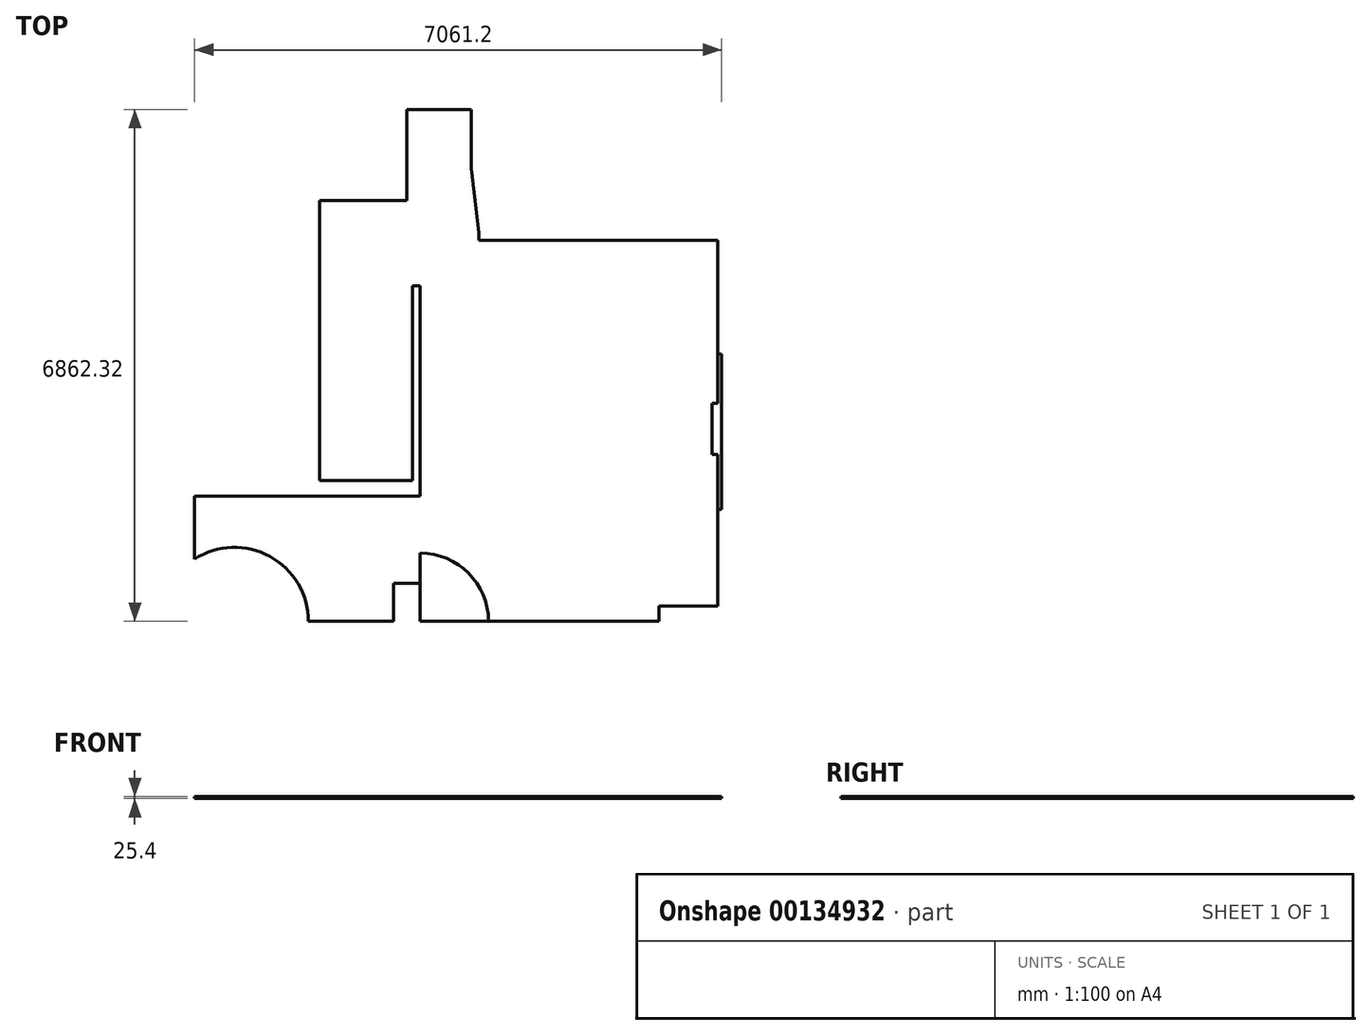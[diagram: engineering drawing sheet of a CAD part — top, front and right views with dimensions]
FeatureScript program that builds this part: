
annotation { "Feature Type Name" : "Feature", "Feature Type Description" : "" }
export const myFeature = defineFeature(function(context is Context, id is Id, definition is map)
    precondition{}
    {
        {
            var Q0;
            Q0=qCreatedBy(makeId("Top.planeOp"),FACE);
            var sketch = newSketch(context, id + "F0", { "sketchPlane" : qUnion([Q0])});
            skLineSegment(sketch, "E0.bottom", {"start": v(3200.4, 0) * mm, "end": v(0, 0) * mm});
            skLineSegment(sketch, "E0.top", {"start": v(3987.8, 5105.4) * mm, "end": v(787.4, 5105.4) * mm});
            skLineSegment(sketch, "E0.left", {"start": v(3987.8, 203.2) * mm, "end": v(3987.8, 5105.4) * mm});
            skLineSegment(sketch, "E0.right", {"start": v(0, 0) * mm, "end": v(0, 508) * mm});
            skLineSegment(sketch, "E1.bottom", {"start": v(-355.6, 0) * mm, "end": v(-3022.6, 0) * mm});
            skLineSegment(sketch, "E1.top", {"start": v(0, 1676.4) * mm, "end": v(-3022.6, 1676.4) * mm});
            skLineSegment(sketch, "E1.left", {"start": v(-355.6, 0) * mm, "end": v(-355.6, 508) * mm});
            skLineSegment(sketch, "E1.right", {"start": v(-3022.6, 0) * mm, "end": v(-3022.6, 1676.4) * mm});
            skLineSegment(sketch, "E2", {"start": v(-355.6, 508) * mm, "end": v(0, 508) * mm});
            skLineSegment(sketch, "E3", {"start": v(3200.4, 0) * mm, "end": v(3200.4, 203.2) * mm});
            skLineSegment(sketch, "E4", {"start": v(3200.4, 203.2) * mm, "end": v(3987.8, 203.2) * mm});
            skLineSegment(sketch, "E5", {"start": v(3987.8, 2235.2) * mm, "end": v(3911.6, 2235.2) * mm});
            skLineSegment(sketch, "E6", {"start": v(3911.6, 2235.2) * mm, "end": v(3911.6, 2921) * mm});
            skLineSegment(sketch, "E7", {"start": v(3911.6, 2921) * mm, "end": v(3987.8, 2921) * mm});
            skLineSegment(sketch, "E8", {"start": v(3987.8, 3581.4) * mm, "end": v(4038.6, 3581.4) * mm});
            skLineSegment(sketch, "E9", {"start": v(4038.6, 3581.4) * mm, "end": v(4038.6, 1498.6) * mm});
            skLineSegment(sketch, "E10", {"start": v(4038.6, 1498.6) * mm, "end": v(3987.8, 1498.6) * mm});
            skLineSegment(sketch, "E11.bottom", {"start": v(685.8, 9550.4) * mm, "end": v(3962.4, 9550.4) * mm});
            skLineSegment(sketch, "E11.top", {"start": v(787.4, 5207) * mm, "end": v(3962.4, 5207) * mm});
            skLineSegment(sketch, "E11.right", {"start": v(3962.4, 9550.4) * mm, "end": v(3962.4, 5207) * mm});
            skLineSegment(sketch, "E12", {"start": v(1778, 5207) * mm, "end": v(1778, 5969) * mm});
            skLineSegment(sketch, "E13", {"start": v(1778, 5969) * mm, "end": v(1981.2, 5969) * mm});
            skLineSegment(sketch, "E14", {"start": v(1981.2, 5969) * mm, "end": v(1981.2, 5207) * mm});
            skLineSegment(sketch, "E15", {"start": v(3810, 5969) * mm, "end": v(3810, 5207) * mm});
            skLineSegment(sketch, "E16", {"start": v(685.8, 9550.4) * mm, "end": v(685.8, 6070.6) * mm});
            skLineSegment(sketch, "E17", {"start": v(685.8, 6070.6) * mm, "end": v(787.4, 5207) * mm});
            skLineSegment(sketch, "E18", {"start": v(787.4, 5207) * mm, "end": v(787.4, 5105.4) * mm});
            skArc(sketch, "E19", {"start": v(701.33, 5938.55) * mm, "mid": v(1276.88, 5757.44) * mm, "end": v(1524, 5207) * mm});
            skLineSegment(sketch, "E20.bottom", {"start": v(-3505.2, 10033) * mm, "end": v(-76.2, 10033) * mm});
            skLineSegment(sketch, "E20.top", {"start": v(-3505.2, 5740.4) * mm, "end": v(-2108.2, 5740.4) * mm});
            skLineSegment(sketch, "E20.left", {"start": v(-3505.2, 10033) * mm, "end": v(-3505.2, 5740.4) * mm});
            skLineSegment(sketch, "E20.right", {"start": v(-177.8, 8839.2) * mm, "end": v(-177.8, 5740.4) * mm});
            skLineSegment(sketch, "E21", {"start": v(-2514.6, 10033) * mm, "end": v(-2514.6, 10083.8) * mm});
            skLineSegment(sketch, "E22", {"start": v(-2514.6, 10083.8) * mm, "end": v(-1028.7, 10083.8) * mm});
            skLineSegment(sketch, "E23", {"start": v(-1028.7, 10083.8) * mm, "end": v(-1028.7, 10033) * mm});
            skLineSegment(sketch, "E24", {"start": v(-2057.4, 10033) * mm, "end": v(-2057.4, 9956.8) * mm});
            skLineSegment(sketch, "E25", {"start": v(-2057.4, 9956.8) * mm, "end": v(-1397, 9956.8) * mm});
            skLineSegment(sketch, "E26", {"start": v(-1397, 9956.8) * mm, "end": v(-1397, 10033) * mm});
            skArc(sketch, "E27", {"start": v(-1498.6, 0) * mm, "mid": v(-2013.33, 868.81) * mm, "end": v(-3022.6, 834.73) * mm});
            skLineSegment(sketch, "E28.bottom", {"start": v(-3840.05, 5638.8) * mm, "end": v(-2108.2, 5638.8) * mm});
            skLineSegment(sketch, "E28.top", {"start": v(-3840.05, 3964.94) * mm, "end": v(-1447.8, 3964.94) * mm});
            skLineSegment(sketch, "E28.left", {"start": v(-3840.05, 5638.8) * mm, "end": v(-3840.05, 3964.94) * mm});
            skLineSegment(sketch, "E28.right", {"start": v(-1447.8, 5638.8) * mm, "end": v(-1447.8, 3964.94) * mm});
            skLineSegment(sketch, "E29.top", {"start": v(-1346.2, 1888.18) * mm, "end": v(-101.6, 1888.18) * mm});
            skLineSegment(sketch, "E29.left", {"start": v(-1346.2, 5638.8) * mm, "end": v(-1346.2, 1888.18) * mm});
            skLineSegment(sketch, "E29.right", {"start": v(-101.6, 4495.8) * mm, "end": v(-101.6, 1888.18) * mm});
            skLineSegment(sketch, "E30.bottom", {"start": v(-3989.7, 1923.09) * mm, "end": v(-1601.5, 1923.09) * mm});
            skLineSegment(sketch, "E30.top", {"start": v(-3989.7, 3685.8) * mm, "end": v(-1601.5, 3685.8) * mm});
            skLineSegment(sketch, "E30.left", {"start": v(-3989.7, 1923.09) * mm, "end": v(-3989.7, 3685.8) * mm});
            skLineSegment(sketch, "E30.right", {"start": v(-1601.5, 1923.09) * mm, "end": v(-1601.5, 3685.8) * mm});
            skLineSegment(sketch, "E31.trimOffspring", {"start": v(0, 1676.4) * mm, "end": v(0, 4495.8) * mm});
            skLineSegment(sketch, "E32", {"start": v(-101.6, 4495.8) * mm, "end": v(0, 4495.8) * mm});
            skLineSegment(sketch, "E33", {"start": v(-1346.2, 5638.8) * mm, "end": v(-177.8, 5638.8) * mm});
            skArc(sketch, "E34", {"start": v(-177.8, 6477) * mm, "mid": v(-698.65, 6261.25) * mm, "end": v(-914.4, 5740.4) * mm});
            skLineSegment(sketch, "E35", {"start": v(-177.8, 6862.32) * mm, "end": v(685.8, 6862.32) * mm});
            skLineSegment(sketch, "E36", {"start": v(-2108.2, 5638.8) * mm, "end": v(-2108.2, 5740.4) * mm});
            skLineSegment(sketch, "E37", {"start": v(-1498.6, 5638.8) * mm, "end": v(-1498.6, 5740.4) * mm});
            skLineSegment(sketch, "E38", {"start": v(-177.8, 5740.4) * mm, "end": v(-177.8, 5638.8) * mm});
            skLineSegment(sketch, "E39.trimOffspring", {"start": v(-1498.6, 5740.4) * mm, "end": v(-177.8, 5740.4) * mm});
            skLineSegment(sketch, "E40.trimOffspring", {"start": v(-1498.6, 5638.8) * mm, "end": v(-1447.8, 5638.8) * mm});
            skLineSegment(sketch, "E41", {"start": v(-1447.8, 5638.8) * mm, "end": v(-1346.2, 5638.8) * mm, "construction": true});
            skLineSegment(sketch, "E42.bottom", {"start": v(-177.8, 8839.2) * mm, "end": v(244.03, 8839.2) * mm});
            skLineSegment(sketch, "E42.top", {"start": v(-177.8, 7035.8) * mm, "end": v(244.03, 7035.8) * mm});
            skLineSegment(sketch, "E42.left", {"start": v(-177.8, 8839.2) * mm, "end": v(-177.8, 7035.8) * mm});
            skLineSegment(sketch, "E42.right", {"start": v(244.03, 8839.2) * mm, "end": v(244.03, 7035.8) * mm});
            skLineSegment(sketch, "E43.trimOffspring", {"start": v(3810, 5969) * mm, "end": v(3962.4, 5969) * mm});
            skLineSegment(sketch, "E44", {"start": v(1981.2, 5969) * mm, "end": v(3810, 5969) * mm});
            skLineSegment(sketch, "E45", {"start": v(-76.2, 10033) * mm, "end": v(-76.2, 8839.2) * mm});
            skArc(sketch, "E46", {"start": v(914.4, 0) * mm, "mid": v(646.58, 646.58) * mm, "end": v(0, 914.4) * mm});
            skLineSegment(sketch, "E47", {"start": v(0, 914.4) * mm, "end": v(0, 508) * mm});
            skSolve(sketch);
        }
        {
            var Q0;
            {var subQ18=sQuery(id+"F0.wireOp",EDGE,"E0.top");Q0=makeQuery(id+"F0.imprint","IMPRINT",FACE,{"disambiguationData":[TD([[makeQuery(id+"F0.imprint","IMPRINT",EDGE,{"derivedFrom":subQ18}),1.0]])]});}
            extrude(context, id + "F1", {"entities" : qUnion([Q0]), "depth" : 25.4 * mm});
        }
        {
            var Q0;
            {var subQ0=sQuery(id+"F0.wireOp",EDGE,"UQPcxE5x-Bd3T-xkpk-ot3p-LLcBCEcp2OZH");Q0=makeQuery(id+"F0.imprint","IMPRINT",FACE,{"disambiguationData":[TD([[makeQuery(id+"F0.imprint","IMPRINT",EDGE,{"derivedFrom":subQ0}),1.0]])]});}
            var Q1;
            {var subQ0=sQuery(id+"F0.wireOp",EDGE,"E5");Q1=makeQuery(id+"F0.imprint","IMPRINT",FACE,{"disambiguationData":[TD([[makeQuery(id+"F0.imprint","IMPRINT",EDGE,{"derivedFrom":subQ0}),-1.0]])]});}
            var Q2;
            {var subQ0=sQuery(id+"F0.wireOp",EDGE,"E8");Q2=makeQuery(id+"F0.imprint","IMPRINT",FACE,{"disambiguationData":[TD([[makeQuery(id+"F0.imprint","IMPRINT",EDGE,{"derivedFrom":subQ0}),-1.0]])]});}
            extrude(context, id + "F2", {"entities" : qUnion([Q0, Q1, Q2]), "depth" : 25.4 * mm});
        }
        {
            var Q0;
            {var subQ0=sQuery(id+"F0.wireOp",EDGE,"E0.right");Q0=makeQuery(id+"F0.imprint","IMPRINT",FACE,{"disambiguationData":[TD([[makeQuery(id+"F0.imprint","IMPRINT",EDGE,{"derivedFrom":subQ0}),-1.0]])]});}
            extrude(context, id + "F3", {"entities" : qUnion([Q0]), "depth" : 25.4 * mm});
        }
    });
